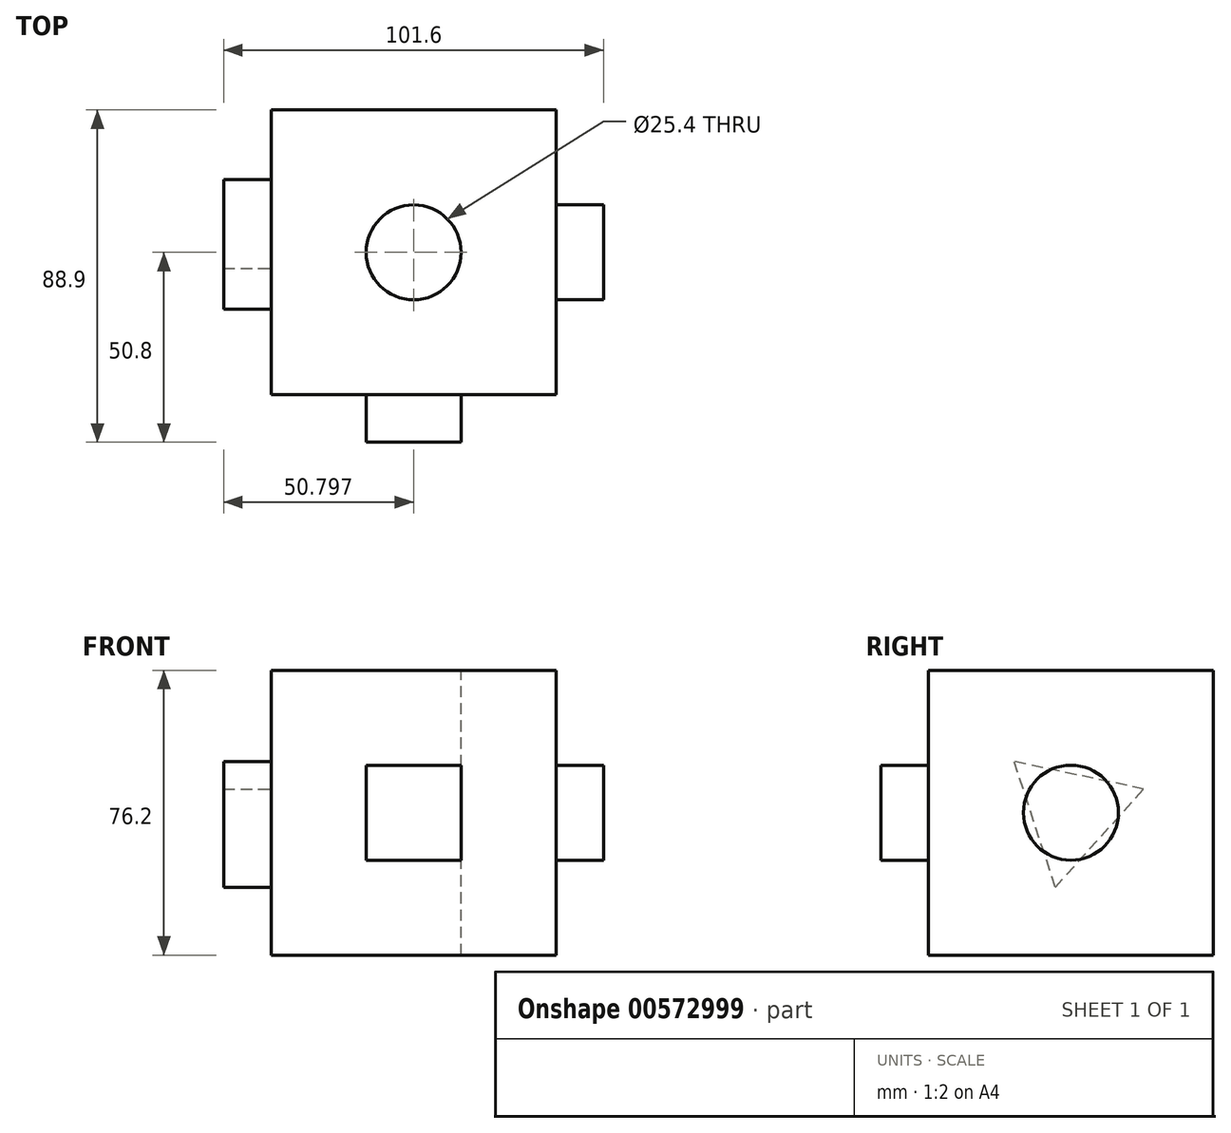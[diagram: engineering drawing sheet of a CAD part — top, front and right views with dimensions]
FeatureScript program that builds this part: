
annotation { "Feature Type Name" : "Feature", "Feature Type Description" : "" }
export const myFeature = defineFeature(function(context is Context, id is Id, definition is map)
    precondition{}
    {
        {
            var Q0;
            Q0=qCreatedBy(makeId("Front.planeOp"),FACE);
            var sketch = newSketch(context, id + "F0", { "sketchPlane" : qUnion([Q0])});
            skLineSegment(sketch, "E0.bottom", {"start": v(-41.6, 42.38) * mm, "end": v(34.6, 42.38) * mm});
            skLineSegment(sketch, "E0.top", {"start": v(-41.6, -33.82) * mm, "end": v(34.6, -33.82) * mm});
            skLineSegment(sketch, "E0.left", {"start": v(-41.6, 42.38) * mm, "end": v(-41.6, -33.82) * mm});
            skLineSegment(sketch, "E0.right", {"start": v(34.6, 42.38) * mm, "end": v(34.6, -33.82) * mm});
            skSolve(sketch);
        }
        {
            var Q0;
            Q0=makeQuery(id+"F0.imprint","IMPRINT",FACE,{"disambiguationData":[TD([[makeQuery(id+"F0.imprint","IMPRINT",EDGE,{"derivedFrom":sQuery(id+"F0.wireOp",EDGE,"E0.bottom")}),-1.0]])]});
            extrude(context, id + "F1", {"entities" : qUnion([Q0]), "depth" : 76.2 * mm, "offsetDistance" : 25.4 * mm});
        }
        {
            var Q0;
            Q0=makeQuery(id+"F1.opExtrude","CAP_FACE",FACE,{"disambiguationData":[OSD([sQuery(id+"F0.wireOp",EDGE,"E0.bottom"),sQuery(id+"F0.wireOp",EDGE,"E0.top"),sQuery(id+"F0.wireOp",EDGE,"E0.left"),sQuery(id+"F0.wireOp",EDGE,"E0.right")])],"isStart":false});
            var sketch = newSketch(context, id + "F2", { "sketchPlane" : qUnion([Q0])});
            skLineSegment(sketch, "E1.bottom", {"start": v(-16.2, 16.98) * mm, "end": v(9.2, 16.98) * mm});
            skLineSegment(sketch, "E1.top", {"start": v(-16.2, -8.42) * mm, "end": v(9.2, -8.42) * mm});
            skLineSegment(sketch, "E1.left", {"start": v(-16.2, 16.98) * mm, "end": v(-16.2, -8.42) * mm});
            skLineSegment(sketch, "E1.right", {"start": v(9.2, 16.98) * mm, "end": v(9.2, -8.42) * mm});
            skSolve(sketch);
        }
        {
            var Q0;
            Q0=makeQuery(id+"F2.imprint","IMPRINT",FACE,{"disambiguationData":[TD([[makeQuery(id+"F2.imprint","IMPRINT",EDGE,{"derivedFrom":sQuery(id+"F2.wireOp",EDGE,"E1.bottom")}),-1.0]])]});
            extrude(context, id + "F3", {"entities" : qUnion([Q0]), "operationType" : NewBodyOperationType.ADD, "depth" : 12.7 * mm, "offsetDistance" : 25.4 * mm});
        }
        {
            var Q0;
            Q0=makeQuery(id+"F1.opExtrude","SWEPT_FACE",FACE,{"disambiguationData":[OSD([sQuery(id+"F0.wireOp",EDGE,"E0.right")])]});
            var sketch = newSketch(context, id + "F4", { "sketchPlane" : qUnion([Q0])});
            skCircle(sketch, "E2", {"center": v(-38.1, 4.28) * mm, "radius": 12.7 * mm});
            skSolve(sketch);
        }
        {
            var Q0;
            Q0=makeQuery(id+"F4.imprint","IMPRINT",FACE,{"disambiguationData":[TD([[makeQuery(id+"F4.imprint","IMPRINT",EDGE,{"derivedFrom":sQuery(id+"F4.wireOp",EDGE,"E2")}),1.0]])]});
            extrude(context, id + "F5", {"entities" : qUnion([Q0]), "operationType" : NewBodyOperationType.ADD, "depth" : 12.7 * mm, "offsetDistance" : 25.4 * mm});
        }
        {
            var Q0;
            Q0=makeQuery(id+"F1.opExtrude","SWEPT_FACE",FACE,{"disambiguationData":[OSD([sQuery(id+"F0.wireOp",EDGE,"E0.bottom")])]});
            var sketch = newSketch(context, id + "F6", { "sketchPlane" : qUnion([Q0])});
            skPoint(sketch, "E3", {"position": v(-3.5, -38.1) * mm});
            skSolve(sketch);
        }
        {
            var Q0;
            Q0=sQuery(id+"F6.wireOp",VERTEX,"E3");
            var Q1;
            Q1=makeQuery(id+"F1.opExtrude","SWEPT_BODY",BODY,{"disambiguationData":[OSD([sQuery(id+"F0.wireOp",EDGE,"E0.bottom"),sQuery(id+"F0.wireOp",EDGE,"E0.top"),sQuery(id+"F0.wireOp",EDGE,"E0.left"),sQuery(id+"F0.wireOp",EDGE,"E0.right")])]});
            hole(context, id + "F7", {"style" : HoleStyle.SIMPLE, "endStyle" : HoleEndStyle.THROUGH, "holeDiameter" : 25.4 * mm, "isTappedThrough" : true, "tappedDepth" : 12.7 * mm, "tapClearance" : 3, "locations" : qUnion([Q0]), "scope" : qUnion([Q1])});
        }
        {
            var Q0;
            Q0=makeQuery(id+"F1.opExtrude","SWEPT_FACE",FACE,{"disambiguationData":[OSD([sQuery(id+"F0.wireOp",EDGE,"E0.left")])]});
            var sketch = newSketch(context, id + "F8", { "sketchPlane" : qUnion([Q0])});
            skCircle(sketch, "E4.cCircle", {"center": v(38.1, 4.28) * mm, "radius": 10.24 * mm, "construction": true});
            skLineSegment(sketch, "E4.0", {"start": v(18.64, 10.63) * mm, "end": v(53.33, 17.96) * mm});
            skLineSegment(sketch, "E4.1", {"start": v(53.33, 17.96) * mm, "end": v(42.33, -15.74) * mm});
            skLineSegment(sketch, "E4.2", {"start": v(42.33, -15.74) * mm, "end": v(18.64, 10.63) * mm});
            skPoint(sketch, "E4.0.midPoint", {"position": v(35.98, 14.3) * mm});
            skSolve(sketch);
        }
        {
            var Q0;
            Q0=makeQuery(id+"F8.imprint","IMPRINT",FACE,{"disambiguationData":[TD([[makeQuery(id+"F8.imprint","IMPRINT",EDGE,{"derivedFrom":sQuery(id+"F8.wireOp",EDGE,"E4.0")}),-1.0]])]});
            extrude(context, id + "F9", {"entities" : qUnion([Q0]), "operationType" : NewBodyOperationType.ADD, "depth" : 12.7 * mm, "offsetDistance" : 25.4 * mm});
        }
    });
